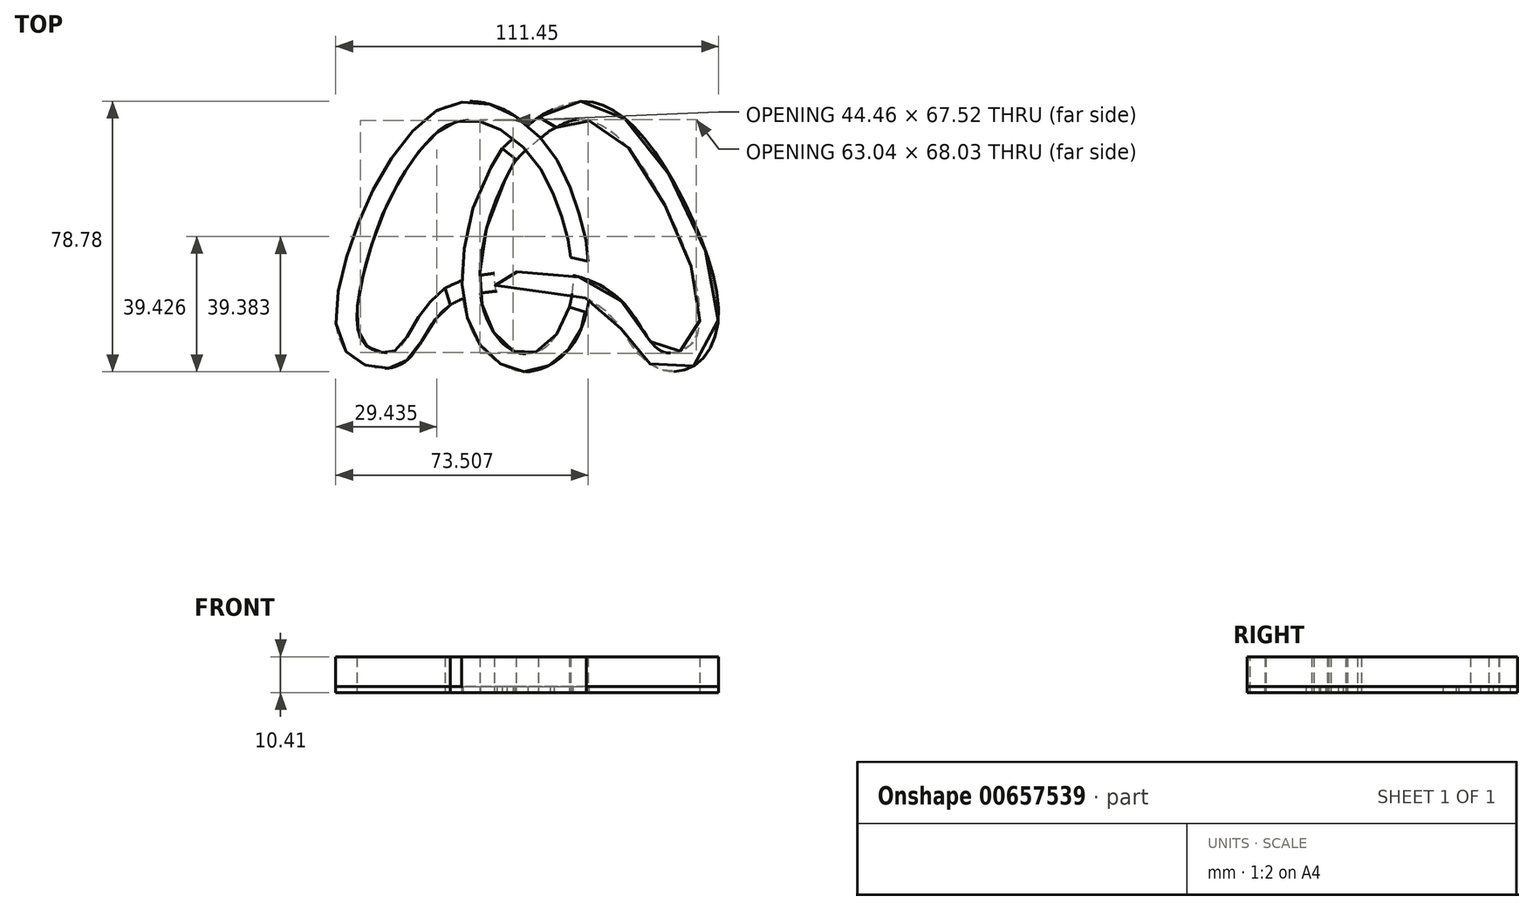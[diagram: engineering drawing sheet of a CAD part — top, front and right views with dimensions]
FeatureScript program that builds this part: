
annotation { "Feature Type Name" : "Feature", "Feature Type Description" : "" }
export const myFeature = defineFeature(function(context is Context, id is Id, definition is map)
    precondition{}
    {
        {
            var Q0;
            Q0=qCreatedBy(makeId("Top.planeOp"),FACE);
            var sketch = newSketch(context, id + "F0", { "sketchPlane" : qUnion([Q0])});
            skFitSpline(sketch, "E0.0", {"points": [v(-23.48, -4.34) * mm, v(-24.02, -4.8) * mm, v(-25.14, -5.77) * mm, v(-26.56, -7.08) * mm, v(-27.7, -8.23) * mm, v(-28.53, -9.16) * mm, v(-29.35, -10.15) * mm, v(-30.14, -11.22) * mm, v(-30.87, -12.31) * mm, v(-31.77, -13.78) * mm, v(-32.82, -15.63) * mm, v(-33.8, -17.38) * mm, v(-34.57, -18.68) * mm, v(-35.33, -19.88) * mm, v(-36.26, -21.16) * mm, v(-37.16, -22.06) * mm, v(-37.86, -22.54) * mm, v(-38.3, -22.77) * mm, v(-38.67, -22.91) * mm, v(-39.05, -23.03) * mm, v(-39.63, -23.14) * mm, v(-40.44, -23.2) * mm, v(-41.33, -23.15) * mm, v(-42.25, -23.02) * mm, v(-43.17, -22.8) * mm, v(-44.06, -22.48) * mm, v(-44.9, -22.1) * mm, v(-45.61, -21.68) * mm, v(-46.45, -21.04) * mm, v(-47.32, -20.1) * mm, v(-48.14, -18.7) * mm, v(-48.64, -17.23) * mm, v(-48.9, -15.87) * mm, v(-49.09, -14.37) * mm, v(-49.14, -12.26) * mm, v(-48.95, -9.4) * mm, v(-48.51, -6.28) * mm, v(-47.86, -2.94) * mm, v(-47.05, 0.58) * mm, v(-46.1, 4.2) * mm, v(-44.99, 7.89) * mm, v(-43.32, 12.84) * mm, v(-41.36, 17.78) * mm, v(-39.1, 22.55) * mm, v(-37.28, 26) * mm, v(-35.32, 29.3) * mm, v(-33.28, 32.4) * mm, v(-31.21, 35.22) * mm, v(-29.15, 37.71) * mm, v(-27.48, 39.46) * mm, v(-26.2, 40.64) * mm, v(-24.99, 41.65) * mm, v(-23.54, 42.66) * mm, v(-21.86, 43.51) * mm, v(-20.14, 44.1) * mm, v(-18.24, 44.45) * mm, v(-16.2, 44.55) * mm, v(-14.07, 44.37) * mm, v(-12.21, 43.95) * mm, v(-10.69, 43.43) * mm, v(-9.13, 42.78) * mm, v(-7.1, 41.7) * mm, v(-4.65, 40.06) * mm, v(-2.27, 38.14) * mm, v(-0.05, 36.03) * mm, v(1.94, 33.84) * mm, v(3.62, 31.64) * mm, v(5.05, 29.39) * mm, v(6.3, 27.05) * mm, v(7.44, 24.58) * mm, v(8.33, 22.4) * mm, v(9.04, 20.56) * mm, v(9.72, 18.69) * mm, v(10.54, 16.33) * mm, v(11.41, 13.59) * mm, v(12, 11.47) * mm, v(12.39, 9.93) * mm, v(12.61, 8.9) * mm, v(12.8, 7.95) * mm, v(12.97, 6.78) * mm, v(13.11, 5.46) * mm, v(13.19, 4.42) * mm, v(13.23, 3.88) * mm]});
            skFitSpline(sketch, "E1.0", {"points": [v(-20.64, -8.14) * mm, v(-21.2, -8.6) * mm, v(-22.3, -9.48) * mm, v(-23.58, -10.61) * mm, v(-24.56, -11.55) * mm, v(-25.26, -12.29) * mm, v(-25.93, -13.06) * mm, v(-26.77, -14.15) * mm, v(-27.82, -15.7) * mm, v(-29.06, -17.76) * mm, v(-30.12, -19.53) * mm, v(-31, -20.94) * mm, v(-31.93, -22.32) * mm, v(-33.2, -23.99) * mm, v(-34.73, -25.48) * mm, v(-36.2, -26.46) * mm, v(-37.22, -26.96) * mm, v(-38.1, -27.27) * mm, v(-39.01, -27.51) * mm, v(-40.18, -27.7) * mm, v(-41.6, -27.75) * mm, v(-43.5, -27.6) * mm, v(-45.39, -27.18) * mm, v(-47.19, -26.5) * mm, v(-48.48, -25.87) * mm, v(-49.7, -25.11) * mm, v(-51.16, -23.94) * mm, v(-52.7, -22.2) * mm, v(-54.02, -19.74) * mm, v(-54.85, -17) * mm, v(-55.22, -14.06) * mm, v(-55.22, -10.94) * mm, v(-54.9, -7.67) * mm, v(-54.33, -4.25) * mm, v(-53.54, -0.7) * mm, v(-52.6, 2.96) * mm, v(-51.49, 6.72) * mm, v(-50.23, 10.54) * mm, v(-48.82, 14.4) * mm, v(-47.25, 18.24) * mm, v(-45.52, 22.06) * mm, v(-43.63, 25.8) * mm, v(-41.58, 29.43) * mm, v(-39.4, 32.89) * mm, v(-37.14, 36.14) * mm, v(-34.82, 39.13) * mm, v(-32.47, 41.81) * mm, v(-30.13, 44.15) * mm, v(-27.82, 46.08) * mm, v(-25.48, 47.62) * mm, v(-23.07, 48.77) * mm, v(-20.99, 49.4) * mm, v(-19.27, 49.74) * mm, v(-17.5, 49.96) * mm, v(-15.2, 50.02) * mm, v(-12.35, 49.7) * mm, v(-9.9, 49.07) * mm, v(-7.93, 48.34) * mm, v(-5.95, 47.45) * mm, v(-3.53, 46.07) * mm, v(-0.72, 44.08) * mm, v(1.94, 41.81) * mm, v(4.4, 39.36) * mm, v(6.23, 37.22) * mm, v(7.55, 35.48) * mm, v(8.75, 33.73) * mm, v(10.08, 31.51) * mm, v(11.44, 28.81) * mm, v(12.62, 26.05) * mm, v(13.5, 23.7) * mm, v(14.2, 21.75) * mm, v(14.86, 19.78) * mm, v(15.65, 17.3) * mm, v(16.49, 14.38) * mm, v(17.06, 12.1) * mm, v(17.44, 10.39) * mm, v(17.75, 8.78) * mm, v(18, 7) * mm, v(18.15, 5.12) * mm, v(18.2, 4) * mm, v(18.22, 3.47) * mm]});
            skLineSegment(sketch, "E2", {"start": v(-23.48, -4.34) * mm, "end": v(-21.93, -9.2) * mm});
            skLineSegment(sketch, "E3", {"start": v(13.17, 4.66) * mm, "end": v(18.22, 3.47) * mm});
            skFitSpline(sketch, "E4", {"points": [v(3.8, 45.45) * mm, v(12, 49.33) * mm, v(22.48, 48.9) * mm, v(34.25, 39.7) * mm, v(50.48, 11.42) * mm, v(56.08, -13.57) * mm, v(50.48, -25.92) * mm, v(40.86, -28.5) * mm, v(32.24, -22.76) * mm, v(26.78, -14.72) * mm, v(18.31, -7.68) * mm, v(4.53, -4.95) * mm, v(-8.4, -5.24) * mm, v(-8.68, -4.8) * mm, v(-9.11, 0) * mm, v(-8.93, 0.06) * mm, v(4.92, 0.47) * mm, v(19.79, -2.61) * mm, v(29.07, -9.33) * mm, v(35.98, -19.36) * mm, v(40.45, -23.02) * mm, v(45.67, -22.4) * mm, v(49.87, -18.4) * mm, v(50.21, -6.34) * mm, v(45.33, 9.72) * mm, v(34.1, 30.98) * mm, v(23.54, 42.25) * mm, v(16.07, 44.77) * mm, v(10.98, 43.55) * mm, v(7.31, 41.68) * mm, v(7.1, 41.9) * mm, v(3.79, 45.35) * mm, v(3.8, 45.45) * mm]});
            skFitSpline(sketch, "E5", {"points": [v(-6.75, 36.4) * mm, v(-4.5, 35) * mm, v(-2.7, 32.93) * mm, v(-2.79, 32.84) * mm, v(-9.85, 18.06) * mm, v(-13.32, -2.2) * mm, v(-12.07, -11.17) * mm, v(-7.78, -19.2) * mm, v(-2.09, -23.19) * mm, v(2.83, -22.95) * mm, v(8.45, -18.74) * mm, v(12.74, -9.92) * mm, v(12.74, -9.89) * mm, v(15.45, -10.35) * mm, v(17.72, -11.53) * mm, v(17.72, -11.63) * mm, v(15.78, -17.18) * mm, v(13.13, -21.56) * mm, v(8.21, -26.03) * mm, v(1.48, -28.59) * mm, v(-4.02, -28) * mm, v(-10.6, -23.92) * mm, v(-15.28, -17.43) * mm, v(-18.23, -7.4) * mm, v(-18.15, 4.92) * mm, v(-14.25, 21.9) * mm, v(-7.75, 35.17) * mm, v(-6.75, 36.4) * mm]});
            skSolve(sketch);
        }
        {
            var Q0;
            Q0=qCreatedBy(makeId("Top.planeOp"),FACE);
            var sketch = newSketch(context, id + "F1", { "sketchPlane" : qUnion([Q0])});
            skFitSpline(sketch, "E6.0", {"points": [v(-23.45, -4.34) * mm, v(-24, -4.8) * mm, v(-25.11, -5.77) * mm, v(-26.54, -7.08) * mm, v(-27.67, -8.23) * mm, v(-28.5, -9.16) * mm, v(-29.32, -10.15) * mm, v(-30.11, -11.22) * mm, v(-30.84, -12.31) * mm, v(-31.75, -13.78) * mm, v(-32.8, -15.63) * mm, v(-33.77, -17.38) * mm, v(-34.54, -18.68) * mm, v(-35.3, -19.88) * mm, v(-36.23, -21.16) * mm, v(-37.13, -22.05) * mm, v(-37.83, -22.54) * mm, v(-38.27, -22.77) * mm, v(-38.64, -22.91) * mm, v(-39.03, -23.03) * mm, v(-39.6, -23.14) * mm, v(-40.41, -23.2) * mm, v(-41.3, -23.15) * mm, v(-42.22, -23.02) * mm, v(-43.14, -22.8) * mm, v(-44.04, -22.48) * mm, v(-44.86, -22.1) * mm, v(-45.59, -21.67) * mm, v(-46.43, -21.04) * mm, v(-47.3, -20.1) * mm, v(-48.11, -18.7) * mm, v(-48.6, -17.23) * mm, v(-48.88, -15.87) * mm, v(-49.06, -14.37) * mm, v(-49.12, -12.26) * mm, v(-48.92, -9.4) * mm, v(-48.48, -6.28) * mm, v(-47.84, -2.94) * mm, v(-47.02, 0.58) * mm, v(-46.07, 4.2) * mm, v(-44.96, 7.89) * mm, v(-43.3, 12.84) * mm, v(-41.33, 17.78) * mm, v(-39.08, 22.55) * mm, v(-37.25, 26) * mm, v(-35.3, 29.3) * mm, v(-33.26, 32.4) * mm, v(-31.18, 35.22) * mm, v(-29.12, 37.71) * mm, v(-27.45, 39.46) * mm, v(-26.18, 40.64) * mm, v(-24.96, 41.66) * mm, v(-23.51, 42.66) * mm, v(-21.83, 43.51) * mm, v(-20.11, 44.1) * mm, v(-18.2, 44.45) * mm, v(-16.18, 44.55) * mm, v(-14.05, 44.37) * mm, v(-12.19, 43.95) * mm, v(-10.66, 43.43) * mm, v(-9.1, 42.78) * mm, v(-7.08, 41.7) * mm, v(-4.62, 40.06) * mm, v(-2.24, 38.14) * mm, v(-0.02, 36.03) * mm, v(1.97, 33.84) * mm, v(3.64, 31.64) * mm, v(5.08, 29.39) * mm, v(6.33, 27.05) * mm, v(7.47, 24.58) * mm, v(8.36, 22.4) * mm, v(9.06, 20.56) * mm, v(9.75, 18.69) * mm, v(10.57, 16.33) * mm, v(11.44, 13.59) * mm, v(12.03, 11.47) * mm, v(12.41, 9.93) * mm, v(12.64, 8.9) * mm, v(12.82, 7.95) * mm, v(13, 6.78) * mm, v(13.14, 5.46) * mm, v(13.22, 4.42) * mm, v(13.26, 3.88) * mm]});
            skFitSpline(sketch, "E7.0", {"points": [v(-20.62, -8.14) * mm, v(-21.17, -8.6) * mm, v(-22.26, -9.48) * mm, v(-23.55, -10.61) * mm, v(-24.53, -11.55) * mm, v(-25.23, -12.29) * mm, v(-25.9, -13.06) * mm, v(-26.75, -14.14) * mm, v(-27.8, -15.7) * mm, v(-29.04, -17.76) * mm, v(-30.1, -19.53) * mm, v(-30.98, -20.94) * mm, v(-31.9, -22.32) * mm, v(-33.17, -23.99) * mm, v(-34.7, -25.47) * mm, v(-36.17, -26.46) * mm, v(-37.2, -26.95) * mm, v(-38.07, -27.27) * mm, v(-38.98, -27.51) * mm, v(-40.15, -27.7) * mm, v(-41.57, -27.75) * mm, v(-43.47, -27.6) * mm, v(-45.36, -27.18) * mm, v(-47.16, -26.5) * mm, v(-48.45, -25.87) * mm, v(-49.67, -25.1) * mm, v(-51.14, -23.94) * mm, v(-52.67, -22.2) * mm, v(-54, -19.74) * mm, v(-54.82, -17) * mm, v(-55.2, -14.06) * mm, v(-55.19, -10.94) * mm, v(-54.87, -7.67) * mm, v(-54.3, -4.25) * mm, v(-53.51, -0.7) * mm, v(-52.56, 2.96) * mm, v(-51.46, 6.72) * mm, v(-50.2, 10.54) * mm, v(-48.8, 14.4) * mm, v(-47.22, 18.25) * mm, v(-45.5, 22.06) * mm, v(-43.6, 25.8) * mm, v(-41.55, 29.43) * mm, v(-39.38, 32.89) * mm, v(-37.11, 36.14) * mm, v(-34.8, 39.13) * mm, v(-32.45, 41.81) * mm, v(-30.1, 44.15) * mm, v(-27.79, 46.09) * mm, v(-25.45, 47.62) * mm, v(-23.04, 48.77) * mm, v(-20.96, 49.4) * mm, v(-19.24, 49.74) * mm, v(-17.48, 49.96) * mm, v(-15.18, 50.02) * mm, v(-12.32, 49.7) * mm, v(-9.87, 49.07) * mm, v(-7.9, 48.34) * mm, v(-5.93, 47.45) * mm, v(-3.5, 46.07) * mm, v(-0.7, 44.08) * mm, v(1.96, 41.81) * mm, v(4.42, 39.36) * mm, v(6.26, 37.22) * mm, v(7.57, 35.48) * mm, v(8.78, 33.73) * mm, v(10.1, 31.51) * mm, v(11.47, 28.81) * mm, v(12.65, 26.05) * mm, v(13.54, 23.7) * mm, v(14.22, 21.75) * mm, v(14.89, 19.78) * mm, v(15.67, 17.3) * mm, v(16.51, 14.38) * mm, v(17.1, 12.1) * mm, v(17.47, 10.39) * mm, v(17.77, 8.78) * mm, v(18.03, 7) * mm, v(18.18, 5.13) * mm, v(18.23, 4) * mm, v(18.25, 3.47) * mm]});
            skLineSegment(sketch, "E8", {"start": v(-23.45, -4.34) * mm, "end": v(-21.9, -9.2) * mm});
            skLineSegment(sketch, "E9", {"start": v(13.2, 4.66) * mm, "end": v(18.25, 3.47) * mm});
            skFitSpline(sketch, "E10", {"points": [v(3.84, 45.45) * mm, v(12.02, 49.33) * mm, v(22.5, 48.9) * mm, v(34.28, 39.7) * mm, v(50.5, 11.42) * mm, v(56.1, -13.57) * mm, v(50.5, -25.92) * mm, v(40.88, -28.5) * mm, v(32.27, -22.76) * mm, v(26.81, -14.72) * mm, v(18.34, -7.68) * mm, v(4.56, -4.95) * mm, v(-8.37, -5.24) * mm, v(-8.66, -4.8) * mm, v(-9.09, 0) * mm, v(-8.9, 0.06) * mm, v(4.94, 0.47) * mm, v(19.81, -2.61) * mm, v(29.1, -9.33) * mm, v(36, -19.36) * mm, v(40.48, -23.02) * mm, v(45.7, -22.4) * mm, v(49.9, -18.4) * mm, v(50.24, -6.34) * mm, v(45.36, 9.72) * mm, v(34.12, 30.98) * mm, v(23.57, 42.25) * mm, v(16.1, 44.77) * mm, v(11, 43.55) * mm, v(7.34, 41.68) * mm, v(7.13, 41.9) * mm, v(3.81, 45.35) * mm, v(3.84, 45.45) * mm]});
            skFitSpline(sketch, "E11", {"points": [v(-6.72, 36.4) * mm, v(-4.46, 35) * mm, v(-2.67, 32.93) * mm, v(-2.76, 32.84) * mm, v(-9.82, 18.06) * mm, v(-13.3, -2.2) * mm, v(-12.05, -11.17) * mm, v(-7.75, -19.2) * mm, v(-2.06, -23.19) * mm, v(2.86, -22.95) * mm, v(8.47, -18.74) * mm, v(12.76, -9.92) * mm, v(12.77, -9.89) * mm, v(15.48, -10.35) * mm, v(17.74, -11.53) * mm, v(17.74, -11.63) * mm, v(15.81, -17.18) * mm, v(13.16, -21.56) * mm, v(8.24, -26.03) * mm, v(1.5, -28.59) * mm, v(-4, -28) * mm, v(-10.58, -23.92) * mm, v(-15.25, -17.43) * mm, v(-18.2, -7.4) * mm, v(-18.12, 4.92) * mm, v(-14.22, 21.9) * mm, v(-7.73, 35.17) * mm, v(-6.72, 36.4) * mm]});
            skFitSpline(sketch, "E12", {"points": [v(-6.72, 36.4) * mm, v(3.84, 45.45) * mm, v(8.33, 47.87) * mm], "startDerivative": vector(18.52, 17.07) * mm, "endDerivative": vector(10.98, 4.85) * mm});
            skFitSpline(sketch, "E13", {"points": [v(7.34, 41.68) * mm, v(-2.67, 32.93) * mm, v(-5.39, 28.33) * mm], "startDerivative": vector(-19.22, -15.04) * mm, "endDerivative": vector(-5.2, -11.39) * mm});
            skFitSpline(sketch, "E14", {"points": [v(-23.45, -4.34) * mm, v(-16.57, -1.45) * mm, v(-9.09, 0) * mm], "startDerivative": vector(13.58, 6.52) * mm, "endDerivative": vector(15.15, 2.16) * mm});
            skFitSpline(sketch, "E15", {"points": [v(-21.9, -9.2) * mm, v(-15.5, -6.37) * mm, v(-8.37, -5.24) * mm], "startDerivative": vector(12.6, 6.56) * mm, "endDerivative": vector(14.47, 1.38) * mm});
            skFitSpline(sketch, "E16", {"points": [v(12.77, -9.89) * mm, v(13.85, -3.27) * mm, v(13.2, 4.66) * mm], "startDerivative": vector(3.08, 13.5) * mm, "endDerivative": vector(-2.15, 15.57) * mm});
            skFitSpline(sketch, "E17", {"points": [v(18.25, 3.47) * mm, v(18.77, -4.8) * mm, v(17.74, -11.53) * mm], "startDerivative": vector(1.82, -16.2) * mm, "endDerivative": vector(-2.92, -13.75) * mm});
            skSolve(sketch);
        }
        {
            var Q0;
            Q0 = qSketchRegion(id + "F1", true);
            var Q1;
            {var subQ0=sQuery(id+"F1.wireOp",EDGE,"E12");var subQ1=sQuery(id+"F1.wireOp",EDGE,"E6.0");var subQ2=makeQuery(id+"F1.imprint","INTERSECT",VERTEX,{"derivedFrom":[subQ1,subQ0]});Q1=makeQuery(id+"F1.imprint","IMPRINT",FACE,{"disambiguationData":[TD([[makeQuery(id+"F1.imprint","IMPRINT",EDGE,{"disambiguationData":[TD([[subQ2,-1.0]])],"derivedFrom":subQ1}),-1.0]])]});}
            var Q2;
            {var subQ1=sQuery(id+"F1.wireOp",EDGE,"E11");var subQ7=makeQuery(id+"F1.imprint","INTERSECT",VERTEX,{"derivedFrom":[subQ1,sQuery(id+"F1.wireOp",EDGE,"E12")]});Q2=makeQuery(id+"F1.imprint","IMPRINT",FACE,{"disambiguationData":[TD([[makeQuery(id+"F1.imprint","IMPRINT",EDGE,{"disambiguationData":[TD([[subQ7,-1.0]])],"derivedFrom":subQ1}),-1.0]])]});}
            var Q3;
            Q3=makeQuery(id+"F0.imprint","IMPRINT",FACE,{"disambiguationData":[TD([[makeQuery(id+"F0.imprint","IMPRINT",EDGE,{"derivedFrom":sQuery(id+"F0.wireOp",EDGE,"E0.0")}),1.0]])]});
            var Q4;
            {var subQ0=sQuery(id+"F1.wireOp",EDGE,"E9");Q4=makeQuery(id+"F1.imprint","IMPRINT",FACE,{"disambiguationData":[TD([[makeQuery(id+"F1.imprint","IMPRINT",EDGE,{"derivedFrom":subQ0}),-1.0]])]});}
            var Q5;
            {var subQ0=sQuery(id+"F1.wireOp",EDGE,"E14");var subQ1=sQuery(id+"F1.wireOp",EDGE,"E10");var subQ2=makeQuery(id+"F1.imprint","INTERSECT",VERTEX,{"derivedFrom":[subQ1,subQ0]});Q5=makeQuery(id+"F1.imprint","IMPRINT",FACE,{"disambiguationData":[TD([[makeQuery(id+"F1.imprint","IMPRINT",EDGE,{"disambiguationData":[TD([[subQ2,1.0]])],"derivedFrom":subQ1}),1.0]])]});}
            var Q6;
            Q6=makeQuery(id+"F0.imprint","IMPRINT",FACE,{"disambiguationData":[TD([[makeQuery(id+"F0.imprint","IMPRINT",EDGE,{"derivedFrom":sQuery(id+"F0.wireOp",EDGE,"E4")}),-1.0]])]});
            extrude(context, id + "F2", {"entities" : qUnion([Q0, Q1, Q2, Q3, Q4, Q5, Q6]), "depth" : 1.78 * mm, "offsetDistance" : 25.4 * mm});
        }
        {
            var Q0;
            Q0 = qSketchRegion(id + "F0", true);
            extrude(context, id + "F3", {"entities" : qUnion([Q0]), "depth" : 10.4 * mm, "offsetDistance" : 25.4 * mm});
        }
    });
